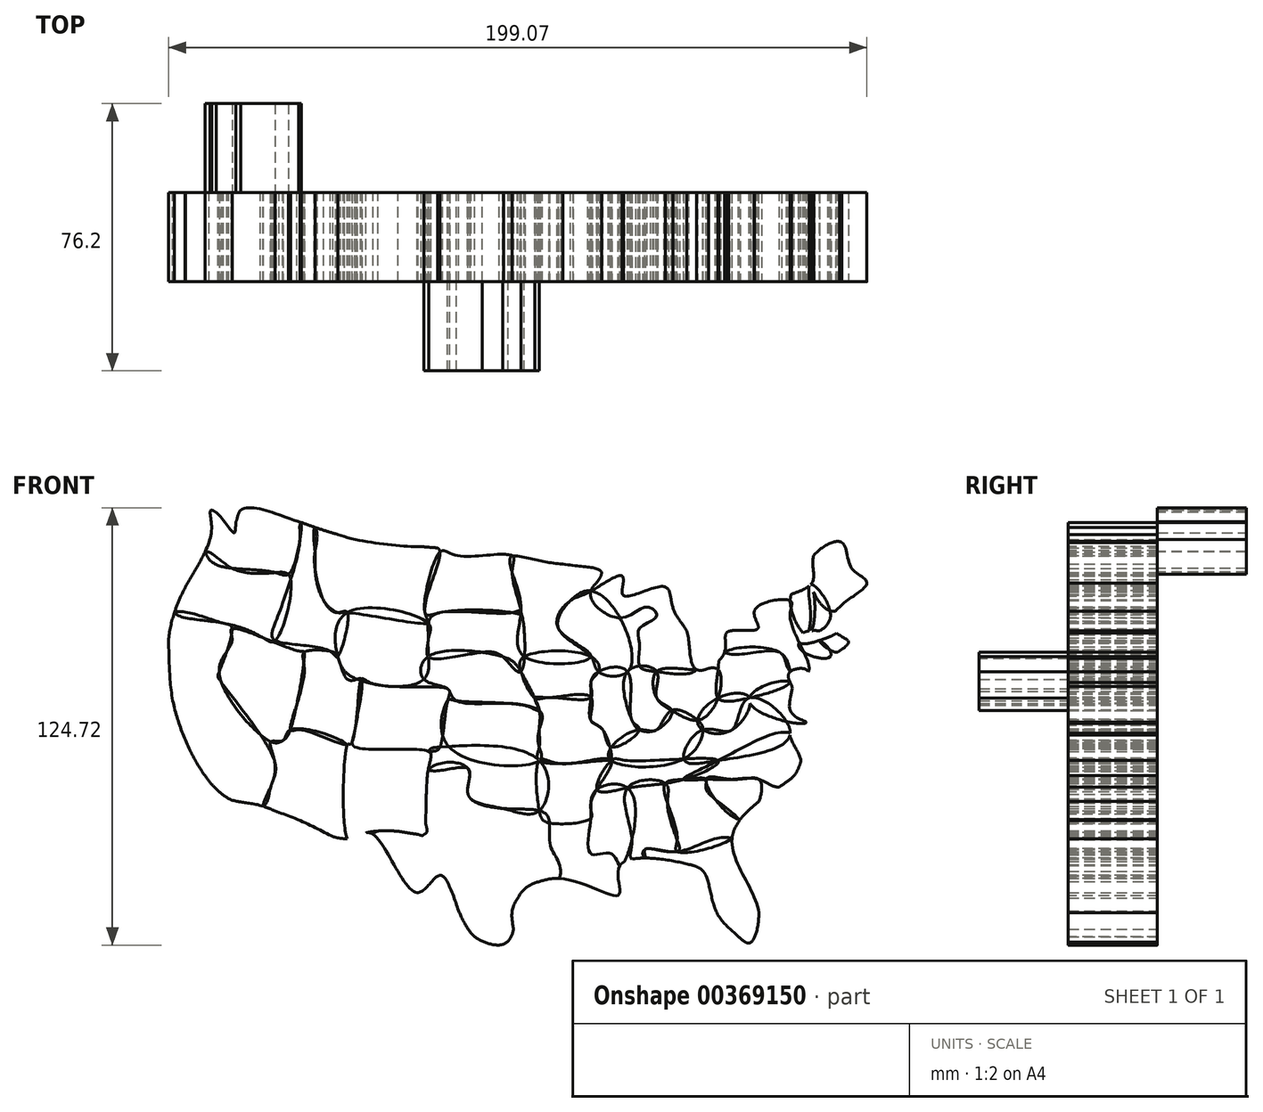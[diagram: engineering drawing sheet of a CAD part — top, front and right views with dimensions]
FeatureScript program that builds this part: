
annotation { "Feature Type Name" : "Feature", "Feature Type Description" : "" }
export const myFeature = defineFeature(function(context is Context, id is Id, definition is map)
    precondition{}
    {
        {
            var Q0;
            Q0=qCreatedBy(makeId("Front.planeOp"),FACE);
            var sketch = newSketch(context, id + "F0", { "sketchPlane" : qUnion([Q0])});
            skFitSpline(sketch, "E0", {"points": [v(64.5, -50.22) * mm, v(58.36, -43.46) * mm, v(55.29, -33.02) * mm, v(50.37, -29.64) * mm, v(30.71, -29.95) * mm, v(30.4, -38.24) * mm, v(13.2, -33.63) * mm, v(0, -42.85) * mm, v(0, -50.83) * mm, v(-10.75, -50.22) * mm, v(-20.58, -32.71) * mm, v(-27.03, -37.62) * mm, v(-39.62, -21.04) * mm, v(-47, -22.27) * mm, v(-70.95, -13.05) * mm, v(-80.78, -10.9) * mm, v(-90.3, 0) * mm, v(-96.75, 17.05) * mm, v(-97.98, 34.25) * mm, v(-93.06, 49.6) * mm, v(-85.7, 65.88) * mm, v(-85.7, 71.41) * mm, v(-79.24, 67.72) * mm, v(-77.4, 71.41) * mm, v(-56.2, 66.5) * mm, v(-32.56, 61.58) * mm, v(0, 58.51) * mm, v(14.44, 56.05) * mm, v(25.5, 53.6) * mm, v(22.42, 48.37) * mm, v(31.33, 52.67) * mm, v(31.64, 47.15) * mm, v(43.3, 49.6) * mm, v(45.76, 43.77) * mm, v(49.76, 37.01) * mm, v(52.52, 25.95) * mm, v(60.5, 30.87) * mm, v(61.43, 36.7) * mm, v(70.03, 37.62) * mm, v(69.1, 42.85) * mm, v(85.08, 50.22) * mm, v(86, 58.51) * mm, v(93.98, 62.2) * mm, v(96.75, 54.82) * mm, v(101.1, 50.52) * mm, v(92.14, 42.54) * mm, v(92.45, 36.4) * mm, v(95.83, 33.63) * mm, v(84.46, 25.34) * mm, v(82.93, 18.27) * mm, v(83.85, 10.9) * mm, v(79.24, 7.83) * mm, v(82.31, 0) * mm, v(76.17, -7.52) * mm, v(62.66, -22.27) * mm, v(70.34, -43.46) * mm, v(67.57, -52.06) * mm, v(64.5, -50.22) * mm]});
            skFitSpline(sketch, "E1", {"points": [v(-39.62, -21.04) * mm, v(-25.16, -21.04) * mm, v(-24.86, -17.35) * mm, v(-23.93, -2.61) * mm, v(-12.57, -2.3) * mm, v(-12.57, -9.67) * mm, v(-2.74, -13.67) * mm, v(7.7, -14.28) * mm, v(10.46, -16.74) * mm, v(10.77, -23.8) * mm, v(13.2, -29.02) * mm, v(13.2, -33.63) * mm, v(7.8, -34.54) * mm, v(1.66, -39.16) * mm, v(0.37, -48.1) * mm, v(-2.75, -52.46) * mm, v(-10.75, -50.22) * mm, v(-15.27, -42.85) * mm, v(-20.58, -32.71) * mm, v(-27.03, -37.62) * mm, v(-39.62, -21.04) * mm]});
            skFitSpline(sketch, "E2", {"points": [v(-47, -22.27) * mm, v(-47, 4.45) * mm, v(-44.82, 3.84) * mm, v(-23.93, 2.61) * mm, v(-23.93, -2.61) * mm, v(-25.16, -21.04) * mm, v(-27.03, -21.03) * mm, v(-43.02, -21.04) * mm, v(-47, -22.27) * mm]});
            skFitSpline(sketch, "E3", {"points": [v(-70.95, -13.05) * mm, v(-67.55, -2.61) * mm, v(-68.78, 5.37) * mm, v(-65.4, 5.68) * mm, v(-63.25, 8.75) * mm, v(-47, 4.45) * mm, v(-47.73, 0) * mm, v(-47, -22.27) * mm, v(-51.07, -21.72) * mm, v(-66.46, -14.89) * mm, v(-70.95, -13.05) * mm]});
            skFitSpline(sketch, "E4", {"points": [v(-67.79, 0) * mm, v(-83.52, 23.19) * mm, v(-83.52, 25.34) * mm, v(-79.83, 37.62) * mm, v(-82.3, 39.16) * mm, v(-96.29, 42.18) * mm, v(-97.98, 34.25) * mm, v(-96.75, 17.05) * mm, v(-90.3, 0) * mm, v(-80.78, -10.9) * mm, v(-70.95, -13.05) * mm, v(-68.78, -7.33) * mm, v(-67.79, 0) * mm]});
            skFitSpline(sketch, "E5", {"points": [v(-63.25, 8.75) * mm, v(-59.26, 30.87) * mm, v(-60.48, 31.17) * mm, v(-79.83, 37.62) * mm, v(-79.83, 34.25) * mm, v(-83.52, 25.34) * mm, v(-68.78, 5.37) * mm, v(-65.4, 5.68) * mm, v(-63.25, 8.75) * mm]});
            skFitSpline(sketch, "E6", {"points": [v(-67.55, 34.25) * mm, v(-63.25, 52.06) * mm, v(-67.55, 53.6) * mm, v(-79.83, 54.82) * mm, v(-87.53, 59.51) * mm, v(-93.06, 49.6) * mm, v(-96.29, 42.18) * mm, v(-82.3, 39.16) * mm, v(-70.95, 34.98) * mm, v(-67.55, 34.25) * mm]});
            skFitSpline(sketch, "E7", {"points": [v(-63.25, 53.6) * mm, v(-60.07, 67.88) * mm, v(-60.81, 68.15) * mm, v(-77.4, 71.41) * mm, v(-79.24, 64.96) * mm, v(-85.7, 71.41) * mm, v(-87.53, 59.51) * mm, v(-79.83, 54.82) * mm, v(-67.55, 53.6) * mm, v(-63.25, 53.6) * mm]});
            skFitSpline(sketch, "E8", {"points": [v(-60.07, 67.88) * mm, v(-56.2, 66.5) * mm, v(-56.2, 59.51) * mm, v(-56.2, 54.82) * mm, v(-53.73, 45.61) * mm, v(-49.73, 42.18) * mm, v(-47, 42.18) * mm, v(-49.73, 29.64) * mm, v(-51.88, 31.17) * mm, v(-67.55, 34.25) * mm, v(-67.55, 39.16) * mm, v(-60.48, 63.07) * mm, v(-60.07, 67.88) * mm]});
            skFitSpline(sketch, "E9", {"points": [v(-56.2, 66.5) * mm, v(-56.2, 59.51) * mm, v(-56.2, 54.82) * mm, v(-53.73, 45.61) * mm, v(-49.73, 42.18) * mm, v(-47, 42.18) * mm, v(-23.93, 39.16) * mm, v(-24.86, 42.18) * mm, v(-20.58, 59.51) * mm, v(-25.16, 60.94) * mm, v(-49.73, 64.48) * mm, v(-56.2, 66.5) * mm]});
            skFitSpline(sketch, "E10", {"points": [v(-49.73, 29.64) * mm, v(-51.88, 31.17) * mm, v(-59.26, 30.87) * mm, v(-59.26, 25.34) * mm, v(-63.25, 8.75) * mm, v(-60.48, 8.75) * mm, v(-47, 4.45) * mm, v(-44.82, 8.75) * mm, v(-42.98, 23.19) * mm, v(-44.2, 23.19) * mm, v(-47, 23.19) * mm, v(-49.73, 29.64) * mm]});
            skFitSpline(sketch, "E11", {"points": [v(-23.93, 39.16) * mm, v(-47, 42.18) * mm, v(-49.73, 29.64) * mm, v(-44.2, 23.19) * mm, v(-25.16, 23.19) * mm, v(-23.93, 34.25) * mm, v(-23.93, 39.16) * mm]});
            skFitSpline(sketch, "E12", {"points": [v(-23.93, 2.61) * mm, v(-44.82, 3.84) * mm, v(-44.82, 8.75) * mm, v(-42.98, 23.19) * mm, v(-39.62, 21.86) * mm, v(-18.4, 20.42) * mm, v(-18.4, 17.05) * mm, v(-20.58, 3.84) * mm, v(-23.93, 2.61) * mm]});
            skFitSpline(sketch, "E13", {"points": [v(-20.58, 3.84) * mm, v(-23.93, 2.61) * mm, v(-23.93, -2.61) * mm, v(-12.57, -2.3) * mm, v(-12.57, -9.67) * mm, v(-2.74, -13.67) * mm, v(7.7, -14.28) * mm, v(7.7, 0) * mm, v(-20.58, 3.84) * mm]});
            skFitSpline(sketch, "E14", {"points": [v(7.7, 0) * mm, v(-18.1, 4) * mm, v(-18.4, 17.05) * mm, v(-15.95, 17.05) * mm, v(7.7, 14.28) * mm, v(7.7, 8.75) * mm, v(7.7, 3.84) * mm, v(7.7, 0) * mm]});
            skFitSpline(sketch, "E15", {"points": [v(7.7, 14.28) * mm, v(2.48, 25.34) * mm, v(-2.74, 29.64) * mm, v(-23.93, 29.64) * mm, v(-25.16, 23.19) * mm, v(-18.4, 20.42) * mm, v(-15.95, 17.05) * mm, v(3.4, 15.78) * mm, v(7.7, 14.28) * mm]});
            skFitSpline(sketch, "E16", {"points": [v(2.48, 25.34) * mm, v(2.48, 42.18) * mm, v(0, 42.18) * mm, v(-20.58, 42.18) * mm, v(-23.93, 39.16) * mm, v(-23.93, 34.25) * mm, v(-23.93, 29.64) * mm, v(-15.95, 29.64) * mm, v(-8.52, 30.87) * mm, v(-2.74, 29.64) * mm, v(2.48, 25.34) * mm]});
            skFitSpline(sketch, "E17", {"points": [v(2.48, 42.18) * mm, v(0, 42.18) * mm, v(-20.58, 42.18) * mm, v(-24.86, 42.18) * mm, v(-20.58, 59.51) * mm, v(-15.95, 58.51) * mm, v(0, 58.51) * mm, v(0, 53.6) * mm, v(2.48, 42.18) * mm]});
            skFitSpline(sketch, "E18", {"points": [v(25.5, 53.6) * mm, v(22.42, 48.37) * mm, v(16.6, 45.61) * mm, v(13.2, 37.62) * mm, v(22.42, 29.64) * mm, v(3.52, 29.64) * mm, v(2.48, 42.18) * mm, v(0, 53.6) * mm, v(0, 58.51) * mm, v(14.44, 56.05) * mm, v(25.5, 53.6) * mm]});
            skFitSpline(sketch, "E19", {"points": [v(22.42, 29.64) * mm, v(3.52, 29.64) * mm, v(2.48, 25.34) * mm, v(6.44, 17.86) * mm, v(10.46, 17.97) * mm, v(22.42, 17.97) * mm, v(22.42, 22.27) * mm, v(24.6, 25.34) * mm, v(22.42, 29.64) * mm]});
            skFitSpline(sketch, "E20", {"points": [v(22.42, 17.97) * mm, v(10.46, 17.97) * mm, v(6.44, 17.86) * mm, v(7.7, 14.28) * mm, v(7.7, 8.75) * mm, v(7.7, 3.84) * mm, v(7.7, 0) * mm, v(25.82, 0) * mm, v(27.97, 0) * mm, v(28.28, 0) * mm, v(25.82, 8.75) * mm, v(22.42, 11.52) * mm, v(22.42, 17.97) * mm]});
            skFitSpline(sketch, "E21", {"points": [v(28.28, 0) * mm, v(22.42, -12.13) * mm, v(22.42, -16.43) * mm, v(10.63, -17.8) * mm, v(7.7, -14.28) * mm, v(7.7, 0) * mm, v(13.88, -0.9) * mm, v(28.28, 0) * mm]});
            skFitSpline(sketch, "E22", {"points": [v(22.42, -16.43) * mm, v(22.42, -26.57) * mm, v(28.28, -26.57) * mm, v(30.71, -29.95) * mm, v(34.11, -22.57) * mm, v(32.89, -7.83) * mm, v(24.2, -8.17) * mm, v(22.42, -12.13) * mm, v(22.42, -16.43) * mm]});
            skFitSpline(sketch, "E23", {"points": [v(28.28, 0) * mm, v(24.2, -8.17) * mm, v(32.89, -7.83) * mm, v(48.86, -5.37) * mm, v(58.69, 0) * mm, v(32.89, 0) * mm, v(28.28, 0) * mm]});
            skFitSpline(sketch, "E24", {"points": [v(43.63, -6.51) * mm, v(32.89, -7.83) * mm, v(34.11, -22.57) * mm, v(34.11, -28.12) * mm, v(37.8, -27.8) * mm, v(37.8, -25.34) * mm, v(47.01, -25.95) * mm, v(47.01, -22.57) * mm, v(44.25, -12.13) * mm, v(43.63, -6.51) * mm]});
            skFitSpline(sketch, "E25", {"points": [v(48.9, 0.47) * mm, v(28.28, 0) * mm, v(28.28, 3.84) * mm, v(36.26, 8.75) * mm, v(41.18, 8.75) * mm, v(45.48, 14.28) * mm, v(52.85, 11.52) * mm, v(54.39, 8.75) * mm, v(48.9, 0.47) * mm]});
            skFitSpline(sketch, "E26", {"points": [v(24.6, 25.34) * mm, v(22.42, 22.27) * mm, v(22.42, 17.97) * mm, v(22.42, 11.52) * mm, v(25.82, 8.75) * mm, v(28.28, 3.84) * mm, v(36.26, 8.75) * mm, v(34.11, 11.52) * mm, v(32.89, 25.34) * mm, v(24.6, 25.34) * mm]});
            skFitSpline(sketch, "E27", {"points": [v(32.89, 25.34) * mm, v(24.6, 25.34) * mm, v(22.42, 29.64) * mm, v(13.2, 37.62) * mm, v(16.6, 45.61) * mm, v(22.42, 48.37) * mm, v(30.71, 40.7) * mm, v(32.89, 25.34) * mm]});
            skFitSpline(sketch, "E28", {"points": [v(45.48, 14.28) * mm, v(41.18, 8.75) * mm, v(36.26, 8.75) * mm, v(34.11, 11.52) * mm, v(32.89, 25.34) * mm, v(41.18, 25.34) * mm, v(41.18, 17.86) * mm, v(45.48, 14.28) * mm]});
            skFitSpline(sketch, "E29", {"points": [v(41.18, 25.34) * mm, v(36.26, 26.95) * mm, v(36.26, 33.32) * mm, v(36.26, 37.62) * mm, v(41.18, 41.31) * mm, v(38.41, 43.77) * mm, v(30.71, 40.7) * mm, v(22.42, 48.37) * mm, v(31.33, 52.67) * mm, v(31.64, 47.15) * mm, v(43.3, 49.6) * mm, v(45.76, 43.77) * mm, v(49.76, 37.01) * mm, v(52.52, 25.95) * mm, v(41.18, 25.34) * mm]});
            skFitSpline(sketch, "E30", {"points": [v(52.85, 11.52) * mm, v(45.48, 14.28) * mm, v(41.18, 17.86) * mm, v(41.18, 25.34) * mm, v(52.52, 25.95) * mm, v(58.69, 25.95) * mm, v(58.69, 17.86) * mm, v(52.85, 11.52) * mm]});
            skFitSpline(sketch, "E31", {"points": [v(47.01, -25.95) * mm, v(37.8, -25.34) * mm, v(37.8, -27.8) * mm, v(50.37, -29.64) * mm, v(55.29, -33.02) * mm, v(58.36, -43.46) * mm, v(64.5, -50.22) * mm, v(67.57, -52.06) * mm, v(70.34, -43.46) * mm, v(62.66, -22.27) * mm, v(47.01, -25.95) * mm]});
            skFitSpline(sketch, "E32", {"points": [v(47.01, -25.95) * mm, v(47.01, -22.57) * mm, v(44.25, -12.13) * mm, v(43.63, -6.51) * mm, v(48.86, -5.37) * mm, v(55.29, -5.37) * mm, v(55.29, -8.17) * mm, v(64.5, -16.74) * mm, v(62.66, -22.27) * mm, v(47.01, -25.95) * mm]});
            skFitSpline(sketch, "E33", {"points": [v(64.5, -16.74) * mm, v(55.29, -5.37) * mm, v(62.66, -5.37) * mm, v(70.34, -5.37) * mm, v(70.34, -11.67) * mm, v(64.5, -16.74) * mm]});
            skFitSpline(sketch, "E34", {"points": [v(58.69, 0) * mm, v(48.86, -5.37) * mm, v(55.29, -5.37) * mm, v(62.66, -5.37) * mm, v(70.34, -5.37) * mm, v(76.17, -7.52) * mm, v(82.31, 0) * mm, v(79.24, 7.83) * mm, v(58.69, 0) * mm]});
            skFitSpline(sketch, "E35", {"points": [v(79.24, 7.83) * mm, v(58.69, 0) * mm, v(48.9, 0.47) * mm, v(54.39, 8.75) * mm, v(62.66, 8.75) * mm, v(67.57, 17.86) * mm, v(79.24, 7.83) * mm]});
            skFitSpline(sketch, "E36", {"points": [v(67.57, 17.86) * mm, v(58.69, 17.86) * mm, v(52.85, 11.52) * mm, v(54.39, 8.75) * mm, v(62.66, 8.75) * mm, v(67.57, 17.86) * mm]});
            skFitSpline(sketch, "E37", {"points": [v(67.57, 17.86) * mm, v(79.24, 22.27) * mm, v(79.24, 14.28) * mm, v(83.85, 10.9) * mm, v(79.24, 10.9) * mm, v(67.57, 17.86) * mm]});
            skFitSpline(sketch, "E38", {"points": [v(79.24, 22.27) * mm, v(67.57, 17.86) * mm, v(58.69, 17.86) * mm, v(58.69, 25.95) * mm, v(60.5, 30.87) * mm, v(76.17, 30.87) * mm, v(79.24, 25.34) * mm, v(79.24, 22.27) * mm]});
            skFitSpline(sketch, "E39", {"points": [v(84.46, 25.34) * mm, v(82.93, 18.27) * mm, v(79.24, 22.27) * mm, v(79.24, 25.34) * mm, v(84.46, 25.34) * mm]});
            skFitSpline(sketch, "E40", {"points": [v(79.24, 45.61) * mm, v(69.1, 42.85) * mm, v(70.03, 37.62) * mm, v(61.43, 36.7) * mm, v(60.5, 30.87) * mm, v(76.17, 30.87) * mm, v(79.24, 25.34) * mm, v(84.46, 25.34) * mm, v(79.24, 40.7) * mm, v(79.24, 45.61) * mm]});
            skFitSpline(sketch, "E41", {"points": [v(81.82, 33.68) * mm, v(87.56, 34.25) * mm, v(90.67, 29.64) * mm, v(83.17, 30.87) * mm, v(81.82, 33.68) * mm]});
            skFitSpline(sketch, "E42", {"points": [v(92.68, 30.87) * mm, v(90.67, 34.25) * mm, v(87.56, 34.25) * mm, v(92.68, 30.87) * mm]});
            skFitSpline(sketch, "E43", {"points": [v(92.45, 36.4) * mm, v(90.67, 36.7) * mm, v(82.93, 36.4) * mm, v(81.82, 33.68) * mm, v(87.56, 34.25) * mm, v(92.45, 36.4) * mm]});
            skFitSpline(sketch, "E44", {"points": [v(85.08, 50.22) * mm, v(85.08, 36.4) * mm, v(82.93, 36.4) * mm, v(79.24, 45.61) * mm, v(81.82, 50.22) * mm, v(85.08, 50.22) * mm]});
            skFitSpline(sketch, "E45", {"points": [v(85.08, 36.4) * mm, v(90.67, 40.7) * mm, v(85.08, 50.22) * mm, v(85.08, 40.7) * mm, v(85.08, 36.4) * mm]});
            skFitSpline(sketch, "E46", {"points": [v(85.08, 50.22) * mm, v(86, 58.51) * mm, v(93.98, 62.2) * mm, v(96.75, 54.82) * mm, v(101.1, 50.52) * mm, v(92.14, 42.54) * mm, v(85.08, 50.22) * mm]});
            skSolve(sketch);
        }
        {
            var Q0;
            {var subQ0=sQuery(id+"F0.wireOp",EDGE,"E7");var subQ4=sQuery(id+"F0.wireOp",EDGE,"E0");var subQ6=makeQuery(id+"F0.imprint","INTERSECT",VERTEX,{"disambiguationData":[OD(1.0)],"derivedFrom":[subQ4,subQ0]});Q0=makeQuery(id+"F0.imprint","IMPRINT",FACE,{"disambiguationData":[TD([[makeQuery(id+"F0.imprint","IMPRINT",EDGE,{"disambiguationData":[TD([[subQ6,-1.0]])],"derivedFrom":subQ4}),-1.0]])]});}
            extrude(context, id + "F1", {"entities" : qUnion([Q0]), "oppositeDirection" : true, "depth" : 25.4 * mm});
        }
        {
            var Q0;
            {var subQ0=sQuery(id+"F0.wireOp",EDGE,"E6");var subQ14=sQuery(id+"F0.wireOp",EDGE,"E5");var subQ16=makeQuery(id+"F0.imprint","INTERSECT",VERTEX,{"disambiguationData":[OD(0.0)],"derivedFrom":[subQ14,subQ0]});Q0=makeQuery(id+"F0.imprint","IMPRINT",FACE,{"disambiguationData":[TD([[makeQuery(id+"F0.imprint","IMPRINT",EDGE,{"disambiguationData":[TD([[subQ16,-1.0]])],"derivedFrom":subQ14}),-1.0]])]});}
            extrude(context, id + "F2", {"entities" : qUnion([Q0]), "depth" : 25.4 * mm});
        }
        {
            var Q0;
            {var subQ0=sQuery(id+"F0.wireOp",EDGE,"E4");var subQ6=sQuery(id+"F0.wireOp",EDGE,"E0");var subQ15=makeQuery(id+"F0.imprint","INTERSECT",VERTEX,{"disambiguationData":[OD(1.0)],"derivedFrom":[subQ6,subQ0]});Q0=makeQuery(id+"F0.imprint","IMPRINT",FACE,{"disambiguationData":[TD([[makeQuery(id+"F0.imprint","IMPRINT",EDGE,{"disambiguationData":[TD([[subQ15,-1.0]])],"derivedFrom":subQ6}),-1.0]])]});}
            extrude(context, id + "F3", {"entities" : qUnion([Q0]), "depth" : 25.4 * mm});
        }
        {
            var Q0;
            {var subQ1=sQuery(id+"F0.wireOp",EDGE,"E5");var subQ13=sQuery(id+"F0.wireOp",EDGE,"E3");var subQ14=makeQuery(id+"F0.imprint","INTERSECT",VERTEX,{"disambiguationData":[OD(0.0)],"derivedFrom":[subQ13,subQ1]});Q0=makeQuery(id+"F0.imprint","IMPRINT",FACE,{"disambiguationData":[TD([[makeQuery(id+"F0.imprint","IMPRINT",EDGE,{"disambiguationData":[TD([[subQ14,-1.0]])],"derivedFrom":subQ13}),1.0]])]});}
            extrude(context, id + "F4", {"entities" : qUnion([Q0]), "depth" : 25.4 * mm});
        }
        {
            var Q0;
            {var subQ1=sQuery(id+"F0.wireOp",EDGE,"E8");var subQ7=sQuery(id+"F0.wireOp",EDGE,"E6");var subQ17=makeQuery(id+"F0.imprint","INTERSECT",VERTEX,{"disambiguationData":[OD(0.0)],"derivedFrom":[subQ7,subQ1]});Q0=makeQuery(id+"F0.imprint","IMPRINT",FACE,{"disambiguationData":[TD([[makeQuery(id+"F0.imprint","IMPRINT",EDGE,{"disambiguationData":[TD([[subQ17,1.0]])],"derivedFrom":subQ7}),-1.0]])]});}
            extrude(context, id + "F5", {"entities" : qUnion([Q0]), "depth" : 25.4 * mm});
        }
        {
            var Q0;
            {var subQ0=sQuery(id+"F0.wireOp",EDGE,"E4");var subQ1=sQuery(id+"F0.wireOp",EDGE,"E3");var subQ2=makeQuery(id+"F0.imprint","INTERSECT",VERTEX,{"disambiguationData":[OD(0.0)],"derivedFrom":[subQ1,subQ0]});Q0=makeQuery(id+"F0.imprint","IMPRINT",FACE,{"disambiguationData":[TD([[makeQuery(id+"F0.imprint","IMPRINT",EDGE,{"disambiguationData":[TD([[subQ2,-1.0]])],"derivedFrom":subQ1}),-1.0]])]});}
            extrude(context, id + "F6", {"entities" : qUnion([Q0]), "depth" : 25.4 * mm});
        }
        {
            var Q0;
            {var subQ1=sQuery(id+"F0.wireOp",EDGE,"E10");var subQ7=sQuery(id+"F0.wireOp",EDGE,"E5");var subQ8=makeQuery(id+"F0.imprint","INTERSECT",VERTEX,{"disambiguationData":[OD(1.0)],"derivedFrom":[subQ7,subQ1]});Q0=makeQuery(id+"F0.imprint","IMPRINT",FACE,{"disambiguationData":[TD([[makeQuery(id+"F0.imprint","IMPRINT",EDGE,{"disambiguationData":[TD([[subQ8,-1.0]])],"derivedFrom":subQ7}),-1.0]])]});}
            extrude(context, id + "F7", {"entities" : qUnion([Q0]), "depth" : 25.4 * mm});
        }
        {
            var Q0;
            {var subQ0=sQuery(id+"F0.wireOp",EDGE,"E9");var subQ1=sQuery(id+"F0.wireOp",EDGE,"E0");var subQ18=makeQuery(id+"F0.imprint","INTERSECT",VERTEX,{"disambiguationData":[OD(1.0)],"derivedFrom":[subQ1,subQ0]});Q0=makeQuery(id+"F0.imprint","IMPRINT",FACE,{"disambiguationData":[TD([[makeQuery(id+"F0.imprint","IMPRINT",EDGE,{"disambiguationData":[TD([[subQ18,-1.0]])],"derivedFrom":subQ1}),-1.0]])]});}
            extrude(context, id + "F8", {"entities" : qUnion([Q0]), "depth" : 25.4 * mm});
        }
        {
            var Q0;
            {var subQ0=sQuery(id+"F0.wireOp",EDGE,"E2");var subQ10=sQuery(id+"F0.wireOp",EDGE,"E0");var subQ11=makeQuery(id+"F0.imprint","INTERSECT",VERTEX,{"disambiguationData":[OD(0.0)],"derivedFrom":[subQ10,subQ0]});Q0=makeQuery(id+"F0.imprint","IMPRINT",FACE,{"disambiguationData":[TD([[makeQuery(id+"F0.imprint","IMPRINT",EDGE,{"disambiguationData":[TD([[subQ11,1.0]])],"derivedFrom":subQ10}),-1.0]])]});}
            extrude(context, id + "F9", {"entities" : qUnion([Q0]), "operationType" : NewBodyOperationType.ADD, "depth" : 25.4 * mm});
        }
        {
            var Q0;
            {var subQ0=sQuery(id+"F0.wireOp",EDGE,"E13");var subQ2=sQuery(id+"F0.wireOp",EDGE,"E1");var subQ6=makeQuery(id+"F0.imprint","INTERSECT",VERTEX,{"disambiguationData":[OD(1.0)],"derivedFrom":[subQ2,subQ0]});Q0=makeQuery(id+"F0.imprint","IMPRINT",FACE,{"disambiguationData":[TD([[makeQuery(id+"F0.imprint","IMPRINT",EDGE,{"disambiguationData":[TD([[subQ6,-1.0]])],"derivedFrom":subQ2}),1.0]])]});}
            extrude(context, id + "F10", {"entities" : qUnion([Q0]), "depth" : 25.4 * mm});
        }
        {
            var Q0;
            {var subQ0=sQuery(id+"F0.wireOp",EDGE,"E14");var subQ1=sQuery(id+"F0.wireOp",EDGE,"E12");var subQ2=makeQuery(id+"F0.imprint","INTERSECT",VERTEX,{"disambiguationData":[OD(0.0)],"derivedFrom":[subQ1,subQ0]});Q0=makeQuery(id+"F0.imprint","IMPRINT",FACE,{"disambiguationData":[TD([[makeQuery(id+"F0.imprint","IMPRINT",EDGE,{"disambiguationData":[TD([[subQ2,-1.0]])],"derivedFrom":subQ1}),1.0]])]});}
            extrude(context, id + "F11", {"entities" : qUnion([Q0]), "depth" : 25.4 * mm});
        }
        {
            var Q0;
            {var subQ1=sQuery(id+"F0.wireOp",EDGE,"E11");var subQ3=sQuery(id+"F0.wireOp",EDGE,"E15");var subQ11=makeQuery(id+"F0.imprint","INTERSECT",VERTEX,{"disambiguationData":[OD(0.0)],"derivedFrom":[subQ1,subQ3]});Q0=makeQuery(id+"F0.imprint","IMPRINT",FACE,{"disambiguationData":[TD([[makeQuery(id+"F0.imprint","IMPRINT",EDGE,{"disambiguationData":[TD([[subQ11,-1.0]])],"derivedFrom":subQ1}),-1.0]])]});}
            extrude(context, id + "F12", {"entities" : qUnion([Q0]), "depth" : 25.4 * mm});
        }
        {
            var Q0;
            {var subQ1=sQuery(id+"F0.wireOp",EDGE,"E11");var subQ13=sQuery(id+"F0.wireOp",EDGE,"E15");var subQ16=makeQuery(id+"F0.imprint","INTERSECT",VERTEX,{"disambiguationData":[OD(1.0)],"derivedFrom":[subQ1,subQ13]});Q0=makeQuery(id+"F0.imprint","IMPRINT",FACE,{"disambiguationData":[TD([[makeQuery(id+"F0.imprint","IMPRINT",EDGE,{"disambiguationData":[TD([[subQ16,-1.0]])],"derivedFrom":subQ1}),-1.0]])]});}
            extrude(context, id + "F13", {"entities" : qUnion([Q0]), "depth" : 25.4 * mm});
        }
        {
            var Q0;
            Q0=makeQuery(id+"F12.opExtrude","CAP_FACE",FACE,{"disambiguationData":[OSD([sQuery(id+"F0.wireOp",EDGE,"E11"),sQuery(id+"F0.wireOp",EDGE,"E12"),sQuery(id+"F0.wireOp",EDGE,"E14"),sQuery(id+"F0.wireOp",EDGE,"E15"),sQuery(id+"F0.wireOp",EDGE,"E16"),sQuery(id+"F0.wireOp",EDGE,"E19"),sQuery(id+"F0.wireOp",EDGE,"E20")])],"isStart":false});
            extrude(context, id + "F14", {"entities" : qUnion([Q0]), "depth" : 25.4 * mm});
        }
        {
            var Q0;
            {var subQ1=sQuery(id+"F0.wireOp",EDGE,"E20");var subQ13=sQuery(id+"F0.wireOp",EDGE,"E14");var subQ15=makeQuery(id+"F0.imprint","INTERSECT",VERTEX,{"disambiguationData":[OD(1.0)],"derivedFrom":[subQ13,subQ1]});Q0=makeQuery(id+"F0.imprint","IMPRINT",FACE,{"disambiguationData":[TD([[makeQuery(id+"F0.imprint","IMPRINT",EDGE,{"disambiguationData":[TD([[subQ15,-1.0]])],"derivedFrom":subQ13}),1.0]])]});}
            extrude(context, id + "F15", {"entities" : qUnion([Q0]), "depth" : 25.4 * mm});
        }
        {
            var Q0;
            {var subQ0=sQuery(id+"F0.wireOp",EDGE,"E18");var subQ6=sQuery(id+"F0.wireOp",EDGE,"E0");var subQ15=makeQuery(id+"F0.imprint","INTERSECT",VERTEX,{"disambiguationData":[OD(1.0)],"derivedFrom":[subQ6,subQ0]});Q0=makeQuery(id+"F0.imprint","IMPRINT",FACE,{"disambiguationData":[TD([[makeQuery(id+"F0.imprint","IMPRINT",EDGE,{"disambiguationData":[TD([[subQ15,-1.0]])],"derivedFrom":subQ6}),-1.0]])]});}
            extrude(context, id + "F16", {"entities" : qUnion([Q0]), "depth" : 25.4 * mm});
        }
        {
            var Q0;
            {var subQ0=sQuery(id+"F0.wireOp",EDGE,"E22");var subQ1=sQuery(id+"F0.wireOp",EDGE,"E0");var subQ9=makeQuery(id+"F0.imprint","INTERSECT",VERTEX,{"disambiguationData":[OD(0.0)],"derivedFrom":[subQ1,subQ0]});Q0=makeQuery(id+"F0.imprint","IMPRINT",FACE,{"disambiguationData":[TD([[makeQuery(id+"F0.imprint","IMPRINT",EDGE,{"disambiguationData":[TD([[subQ9,-1.0]])],"derivedFrom":subQ1}),-1.0]])]});}
            extrude(context, id + "F17", {"entities" : qUnion([Q0]), "depth" : 25.4 * mm});
        }
        {
            var Q0;
            {var subQ1=sQuery(id+"F0.wireOp",EDGE,"E26");var subQ4=sQuery(id+"F0.wireOp",EDGE,"E20");var subQ5=makeQuery(id+"F0.imprint","INTERSECT",VERTEX,{"disambiguationData":[OD(0.0)],"derivedFrom":[subQ4,subQ1]});Q0=makeQuery(id+"F0.imprint","IMPRINT",FACE,{"disambiguationData":[TD([[makeQuery(id+"F0.imprint","IMPRINT",EDGE,{"disambiguationData":[TD([[subQ5,-1.0]])],"derivedFrom":subQ4}),-1.0]])]});}
            extrude(context, id + "F18", {"entities" : qUnion([Q0]), "depth" : 25.4 * mm});
        }
        {
            var Q0;
            {var subQ0=sQuery(id+"F0.wireOp",EDGE,"E27");var subQ6=sQuery(id+"F0.wireOp",EDGE,"E18");var subQ12=makeQuery(id+"F0.imprint","INTERSECT",VERTEX,{"disambiguationData":[OD(0.0)],"derivedFrom":[subQ6,subQ0]});Q0=makeQuery(id+"F0.imprint","IMPRINT",FACE,{"disambiguationData":[TD([[makeQuery(id+"F0.imprint","IMPRINT",EDGE,{"disambiguationData":[TD([[subQ12,1.0]])],"derivedFrom":subQ0}),-1.0]])]});}
            extrude(context, id + "F19", {"entities" : qUnion([Q0]), "depth" : 25.4 * mm});
        }
        {
            var Q0;
            {var subQ0=sQuery(id+"F0.wireOp",EDGE,"E29");var subQ5=sQuery(id+"F0.wireOp",EDGE,"E0");var subQ10=makeQuery(id+"F0.imprint","INTERSECT",VERTEX,{"disambiguationData":[OD(0.0)],"derivedFrom":[subQ5,subQ0]});Q0=makeQuery(id+"F0.imprint","IMPRINT",FACE,{"disambiguationData":[TD([[makeQuery(id+"F0.imprint","IMPRINT",EDGE,{"disambiguationData":[TD([[subQ10,1.0]])],"derivedFrom":subQ5}),-1.0]])]});}
            extrude(context, id + "F20", {"entities" : qUnion([Q0]), "depth" : 25.4 * mm});
        }
        {
            var Q0;
            {var subQ0=sQuery(id+"F0.wireOp",EDGE,"E28");var subQ11=sQuery(id+"F0.wireOp",EDGE,"E25");var subQ12=makeQuery(id+"F0.imprint","INTERSECT",VERTEX,{"disambiguationData":[OD(0.0)],"derivedFrom":[subQ11,subQ0]});Q0=makeQuery(id+"F0.imprint","IMPRINT",FACE,{"disambiguationData":[TD([[makeQuery(id+"F0.imprint","IMPRINT",EDGE,{"disambiguationData":[TD([[subQ12,1.0]])],"derivedFrom":subQ0}),-1.0]])]});}
            extrude(context, id + "F21", {"entities" : qUnion([Q0]), "depth" : 25.4 * mm});
        }
        {
            var Q0;
            {var subQ0=sQuery(id+"F0.wireOp",EDGE,"E30");var subQ1=sQuery(id+"F0.wireOp",EDGE,"E28");var subQ7=makeQuery(id+"F0.imprint","INTERSECT",VERTEX,{"disambiguationData":[OD(0.0)],"derivedFrom":[subQ1,subQ0]});Q0=makeQuery(id+"F0.imprint","IMPRINT",FACE,{"disambiguationData":[TD([[makeQuery(id+"F0.imprint","IMPRINT",EDGE,{"disambiguationData":[TD([[subQ7,1.0]])],"derivedFrom":subQ0}),-1.0]])]});}
            extrude(context, id + "F22", {"entities" : qUnion([Q0]), "depth" : 25.4 * mm});
        }
        {
            var Q0;
            {var subQ1=sQuery(id+"F0.wireOp",EDGE,"E25");var subQ4=sQuery(id+"F0.wireOp",EDGE,"E20");var subQ5=makeQuery(id+"F0.imprint","INTERSECT",VERTEX,{"derivedFrom":[subQ4,subQ1]});Q0=makeQuery(id+"F0.imprint","IMPRINT",FACE,{"disambiguationData":[TD([[makeQuery(id+"F0.imprint","IMPRINT",EDGE,{"disambiguationData":[TD([[subQ5,-1.0]])],"derivedFrom":subQ1}),-1.0]])]});}
            extrude(context, id + "F23", {"entities" : qUnion([Q0]), "depth" : 25.4 * mm});
        }
        {
            var Q0;
            {var subQ1=sQuery(id+"F0.wireOp",EDGE,"E23");var subQ2=sQuery(id+"F0.wireOp",EDGE,"E22");var subQ8=sQuery(id+"F0.wireOp",EDGE,"E21");var subQ9=makeQuery(id+"F0.imprint","INTERSECT",VERTEX,{"derivedFrom":[subQ8,subQ2,subQ1]});Q0=makeQuery(id+"F0.imprint","IMPRINT",FACE,{"disambiguationData":[TD([[makeQuery(id+"F0.imprint","IMPRINT",EDGE,{"disambiguationData":[TD([[subQ9,1.0]])],"derivedFrom":subQ2}),-1.0]])]});}
            extrude(context, id + "F24", {"entities" : qUnion([Q0]), "depth" : 25.4 * mm});
        }
        {
            var Q0;
            {var subQ1=sQuery(id+"F0.wireOp",EDGE,"E24");var subQ3=sQuery(id+"F0.wireOp",EDGE,"E0");var subQ16=makeQuery(id+"F0.imprint","INTERSECT",VERTEX,{"derivedFrom":[subQ3,subQ1]});Q0=makeQuery(id+"F0.imprint","IMPRINT",FACE,{"disambiguationData":[TD([[makeQuery(id+"F0.imprint","IMPRINT",EDGE,{"disambiguationData":[TD([[subQ16,1.0]])],"derivedFrom":subQ1}),1.0]])]});}
            extrude(context, id + "F25", {"entities" : qUnion([Q0]), "depth" : 25.4 * mm});
        }
        {
            var Q0;
            {var subQ0=sQuery(id+"F0.wireOp",EDGE,"E31");var subQ6=sQuery(id+"F0.wireOp",EDGE,"E0");var subQ12=makeQuery(id+"F0.imprint","INTERSECT",VERTEX,{"disambiguationData":[OD(0.0)],"derivedFrom":[subQ6,subQ0]});Q0=makeQuery(id+"F0.imprint","IMPRINT",FACE,{"disambiguationData":[TD([[makeQuery(id+"F0.imprint","IMPRINT",EDGE,{"disambiguationData":[TD([[subQ12,1.0]])],"derivedFrom":subQ6}),-1.0]])]});}
            extrude(context, id + "F26", {"entities" : qUnion([Q0]), "depth" : 25.4 * mm});
        }
        {
            var Q0;
            {var subQ1=sQuery(id+"F0.wireOp",EDGE,"E32");var subQ11=sQuery(id+"F0.wireOp",EDGE,"E24");var subQ17=makeQuery(id+"F0.imprint","INTERSECT",VERTEX,{"disambiguationData":[OD(0.0)],"derivedFrom":[subQ11,subQ1]});Q0=makeQuery(id+"F0.imprint","IMPRINT",FACE,{"disambiguationData":[TD([[makeQuery(id+"F0.imprint","IMPRINT",EDGE,{"disambiguationData":[TD([[subQ17,-1.0]])],"derivedFrom":subQ1}),-1.0]])]});}
            extrude(context, id + "F27", {"entities" : qUnion([Q0]), "depth" : 25.4 * mm});
        }
        {
            var Q0;
            {var subQ0=sQuery(id+"F0.wireOp",EDGE,"E33");var subQ5=sQuery(id+"F0.wireOp",EDGE,"E0");var subQ6=makeQuery(id+"F0.imprint","INTERSECT",VERTEX,{"disambiguationData":[OD(0.0)],"derivedFrom":[subQ5,subQ0]});Q0=makeQuery(id+"F0.imprint","IMPRINT",FACE,{"disambiguationData":[TD([[makeQuery(id+"F0.imprint","IMPRINT",EDGE,{"disambiguationData":[TD([[subQ6,-1.0]])],"derivedFrom":subQ5}),-1.0]])]});}
            extrude(context, id + "F28", {"entities" : qUnion([Q0]), "depth" : 25.4 * mm});
        }
        {
            var Q0;
            {var subQ0=sQuery(id+"F0.wireOp",EDGE,"E36");var subQ1=sQuery(id+"F0.wireOp",EDGE,"E35");var subQ2=makeQuery(id+"F0.imprint","INTERSECT",VERTEX,{"disambiguationData":[OD(0.0)],"derivedFrom":[subQ1,subQ0]});Q0=makeQuery(id+"F0.imprint","IMPRINT",FACE,{"disambiguationData":[TD([[makeQuery(id+"F0.imprint","IMPRINT",EDGE,{"disambiguationData":[TD([[subQ2,-1.0]])],"derivedFrom":subQ1}),-1.0]])]});}
            extrude(context, id + "F29", {"entities" : qUnion([Q0]), "depth" : 25.4 * mm});
        }
        {
            var Q0;
            {var subQ0=sQuery(id+"F0.wireOp",EDGE,"E34");var subQ6=sQuery(id+"F0.wireOp",EDGE,"E0");var subQ11=makeQuery(id+"F0.imprint","INTERSECT",VERTEX,{"disambiguationData":[OD(0.0)],"derivedFrom":[subQ6,subQ0]});Q0=makeQuery(id+"F0.imprint","IMPRINT",FACE,{"disambiguationData":[TD([[makeQuery(id+"F0.imprint","IMPRINT",EDGE,{"disambiguationData":[TD([[subQ11,1.0]])],"derivedFrom":subQ6}),-1.0]])]});}
            extrude(context, id + "F30", {"entities" : qUnion([Q0]), "depth" : 25.4 * mm});
        }
        {
            var Q0;
            {var subQ0=sQuery(id+"F0.wireOp",EDGE,"E36");var subQ1=sQuery(id+"F0.wireOp",EDGE,"E35");var subQ5=makeQuery(id+"F0.imprint","INTERSECT",VERTEX,{"disambiguationData":[OD(0.0)],"derivedFrom":[subQ1,subQ0]});Q0=makeQuery(id+"F0.imprint","IMPRINT",FACE,{"disambiguationData":[TD([[makeQuery(id+"F0.imprint","IMPRINT",EDGE,{"disambiguationData":[TD([[subQ5,-1.0]])],"derivedFrom":subQ0}),1.0]])]});}
            extrude(context, id + "F31", {"entities" : qUnion([Q0]), "depth" : 25.4 * mm});
        }
        {
            var Q0;
            {var subQ1=sQuery(id+"F0.wireOp",EDGE,"E38");var subQ6=sQuery(id+"F0.wireOp",EDGE,"E0");var subQ7=makeQuery(id+"F0.imprint","INTERSECT",VERTEX,{"derivedFrom":[subQ6,subQ1]});Q0=makeQuery(id+"F0.imprint","IMPRINT",FACE,{"disambiguationData":[TD([[makeQuery(id+"F0.imprint","IMPRINT",EDGE,{"disambiguationData":[TD([[subQ7,1.0]])],"derivedFrom":subQ1}),-1.0]])]});}
            extrude(context, id + "F32", {"entities" : qUnion([Q0]), "depth" : 25.4 * mm});
        }
        {
            var Q0;
            {var subQ0=sQuery(id+"F0.wireOp",EDGE,"E37");var subQ1=sQuery(id+"F0.wireOp",EDGE,"E0");var subQ5=makeQuery(id+"F0.imprint","INTERSECT",VERTEX,{"disambiguationData":[OD(0.0)],"derivedFrom":[subQ1,subQ0]});Q0=makeQuery(id+"F0.imprint","IMPRINT",FACE,{"disambiguationData":[TD([[makeQuery(id+"F0.imprint","IMPRINT",EDGE,{"disambiguationData":[TD([[subQ5,-1.0]])],"derivedFrom":subQ1}),-1.0]])]});}
            extrude(context, id + "F33", {"entities" : qUnion([Q0]), "depth" : 25.4 * mm});
        }
        {
            var Q0;
            {var subQ0=sQuery(id+"F0.wireOp",EDGE,"E41");var subQ1=sQuery(id+"F0.wireOp",EDGE,"E0");var subQ5=makeQuery(id+"F0.imprint","INTERSECT",VERTEX,{"disambiguationData":[OD(0.0)],"derivedFrom":[subQ1,subQ0]});Q0=makeQuery(id+"F0.imprint","IMPRINT",FACE,{"disambiguationData":[TD([[makeQuery(id+"F0.imprint","IMPRINT",EDGE,{"disambiguationData":[TD([[subQ5,-1.0]])],"derivedFrom":subQ1}),-1.0]])]});}
            extrude(context, id + "F34", {"entities" : qUnion([Q0]), "depth" : 25.4 * mm});
        }
        {
            var Q0;
            {var subQ0=sQuery(id+"F0.wireOp",EDGE,"E42");var subQ1=sQuery(id+"F0.wireOp",EDGE,"E0");var subQ5=makeQuery(id+"F0.imprint","INTERSECT",VERTEX,{"disambiguationData":[OD(0.0)],"derivedFrom":[subQ1,subQ0]});Q0=makeQuery(id+"F0.imprint","IMPRINT",FACE,{"disambiguationData":[TD([[makeQuery(id+"F0.imprint","IMPRINT",EDGE,{"disambiguationData":[TD([[subQ5,-1.0]])],"derivedFrom":subQ1}),-1.0]])]});}
            extrude(context, id + "F35", {"entities" : qUnion([Q0]), "depth" : 25.4 * mm});
        }
        {
            var Q0;
            {var subQ0=sQuery(id+"F0.wireOp",EDGE,"E43");var subQ1=sQuery(id+"F0.wireOp",EDGE,"E0");var subQ2=makeQuery(id+"F0.imprint","INTERSECT",VERTEX,{"disambiguationData":[OD(1.0)],"derivedFrom":[subQ1,subQ0]});Q0=makeQuery(id+"F0.imprint","IMPRINT",FACE,{"disambiguationData":[TD([[makeQuery(id+"F0.imprint","IMPRINT",EDGE,{"disambiguationData":[TD([[subQ2,-1.0]])],"derivedFrom":subQ1}),-1.0]])]});}
            extrude(context, id + "F36", {"entities" : qUnion([Q0]), "operationType" : NewBodyOperationType.ADD, "depth" : 25.4 * mm});
        }
        {
            var Q0;
            {var subQ0=sQuery(id+"F0.wireOp",EDGE,"E40");var subQ2=sQuery(id+"F0.wireOp",EDGE,"E0");var subQ7=makeQuery(id+"F0.imprint","INTERSECT",VERTEX,{"disambiguationData":[OD(1.0)],"derivedFrom":[subQ2,subQ0]});Q0=makeQuery(id+"F0.imprint","IMPRINT",FACE,{"disambiguationData":[TD([[makeQuery(id+"F0.imprint","IMPRINT",EDGE,{"disambiguationData":[TD([[subQ7,-1.0]])],"derivedFrom":subQ2}),-1.0]])]});}
            extrude(context, id + "F37", {"entities" : qUnion([Q0]), "depth" : 25.4 * mm});
        }
        {
            var Q0;
            {var subQ0=sQuery(id+"F0.wireOp",EDGE,"E44");var subQ8=sQuery(id+"F0.wireOp",EDGE,"E0");var subQ9=makeQuery(id+"F0.imprint","INTERSECT",VERTEX,{"derivedFrom":[subQ8,subQ0]});Q0=makeQuery(id+"F0.imprint","IMPRINT",FACE,{"disambiguationData":[TD([[makeQuery(id+"F0.imprint","IMPRINT",EDGE,{"disambiguationData":[TD([[subQ9,-1.0]])],"derivedFrom":subQ8}),-1.0]])]});}
            extrude(context, id + "F38", {"entities" : qUnion([Q0]), "depth" : 25.4 * mm});
        }
        {
            var Q0;
            {var subQ0=sQuery(id+"F0.wireOp",EDGE,"E45");var subQ1=sQuery(id+"F0.wireOp",EDGE,"E43");var subQ2=makeQuery(id+"F0.imprint","INTERSECT",VERTEX,{"disambiguationData":[OD(0.0)],"derivedFrom":[subQ1,subQ0]});Q0=makeQuery(id+"F0.imprint","IMPRINT",FACE,{"disambiguationData":[TD([[makeQuery(id+"F0.imprint","IMPRINT",EDGE,{"disambiguationData":[TD([[subQ2,-1.0]])],"derivedFrom":subQ1}),-1.0]])]});}
            extrude(context, id + "F39", {"entities" : qUnion([Q0]), "depth" : 25.4 * mm});
        }
        {
            var Q0;
            {var subQ0=sQuery(id+"F0.wireOp",EDGE,"E46");var subQ3=sQuery(id+"F0.wireOp",EDGE,"E0");var subQ9=makeQuery(id+"F0.imprint","INTERSECT",VERTEX,{"disambiguationData":[OD(0.0)],"derivedFrom":[subQ3,subQ0]});Q0=makeQuery(id+"F0.imprint","IMPRINT",FACE,{"disambiguationData":[TD([[makeQuery(id+"F0.imprint","IMPRINT",EDGE,{"disambiguationData":[TD([[subQ9,1.0]])],"derivedFrom":subQ3}),-1.0]])]});}
            extrude(context, id + "F40", {"entities" : qUnion([Q0]), "depth" : 25.4 * mm});
        }
        {
            var Q0;
            {var subQ0=sQuery(id+"F0.wireOp",EDGE,"E12");var subQ1=sQuery(id+"F0.wireOp",EDGE,"E11");var subQ2=makeQuery(id+"F0.imprint","INTERSECT",VERTEX,{"disambiguationData":[OD(1.0)],"derivedFrom":[subQ1,subQ0]});Q0=makeQuery(id+"F0.imprint","IMPRINT",FACE,{"disambiguationData":[TD([[makeQuery(id+"F0.imprint","IMPRINT",EDGE,{"disambiguationData":[TD([[subQ2,-1.0]])],"derivedFrom":subQ1}),1.0]])]});}
            extrude(context, id + "F41", {"entities" : qUnion([Q0]), "depth" : 25.4 * mm});
        }
        {
            var Q0;
            {var subQ0=sQuery(id+"F0.wireOp",EDGE,"E21");var subQ1=sQuery(id+"F0.wireOp",EDGE,"E20");var subQ2=makeQuery(id+"F0.imprint","INTERSECT",VERTEX,{"disambiguationData":[OD(1.0)],"derivedFrom":[subQ1,subQ0]});Q0=makeQuery(id+"F0.imprint","IMPRINT",FACE,{"disambiguationData":[TD([[makeQuery(id+"F0.imprint","IMPRINT",EDGE,{"disambiguationData":[TD([[subQ2,-1.0]])],"derivedFrom":subQ1}),-1.0]])]});}
            extrude(context, id + "F42", {"entities" : qUnion([Q0]), "depth" : 25.4 * mm});
        }
        {
            var Q0;
            {var subQ0=sQuery(id+"F0.wireOp",EDGE,"E12");var subQ1=sQuery(id+"F0.wireOp",EDGE,"E11");var subQ2=makeQuery(id+"F0.imprint","INTERSECT",VERTEX,{"disambiguationData":[OD(1.0)],"derivedFrom":[subQ1,subQ0]});Q0=makeQuery(id+"F0.imprint","IMPRINT",FACE,{"disambiguationData":[TD([[makeQuery(id+"F0.imprint","IMPRINT",EDGE,{"disambiguationData":[TD([[subQ2,-1.0]])],"derivedFrom":subQ1}),1.0]])]});}
            extrude(context, id + "F43", {"entities" : qUnion([Q0]), "depth" : 25.4 * mm});
        }
        {
            var Q0;
            {var subQ0=sQuery(id+"F0.wireOp",EDGE,"E22");var subQ1=sQuery(id+"F0.wireOp",EDGE,"E0");var subQ2=makeQuery(id+"F0.imprint","INTERSECT",VERTEX,{"disambiguationData":[OD(1.0)],"derivedFrom":[subQ1,subQ0]});Q0=makeQuery(id+"F0.imprint","IMPRINT",FACE,{"disambiguationData":[TD([[makeQuery(id+"F0.imprint","IMPRINT",EDGE,{"disambiguationData":[TD([[subQ2,-1.0]])],"derivedFrom":subQ1}),-1.0]])]});}
            extrude(context, id + "F44", {"entities" : qUnion([Q0]), "depth" : 25.4 * mm});
        }
        {
            var Q0;
            {var subQ0=sQuery(id+"F0.wireOp",EDGE,"E26");var subQ1=sQuery(id+"F0.wireOp",EDGE,"E19");var subQ2=makeQuery(id+"F0.imprint","INTERSECT",VERTEX,{"disambiguationData":[OD(0.0)],"derivedFrom":[subQ1,subQ0]});Q0=makeQuery(id+"F0.imprint","IMPRINT",FACE,{"disambiguationData":[TD([[makeQuery(id+"F0.imprint","IMPRINT",EDGE,{"disambiguationData":[TD([[subQ2,-1.0]])],"derivedFrom":subQ1}),1.0]])]});}
            extrude(context, id + "F45", {"entities" : qUnion([Q0]), "depth" : 25.4 * mm});
        }
        {
            var Q0;
            {var subQ0=sQuery(id+"F0.wireOp",EDGE,"E17");var subQ4=sQuery(id+"F0.wireOp",EDGE,"E9");var subQ5=makeQuery(id+"F0.imprint","INTERSECT",VERTEX,{"disambiguationData":[OD(0.0)],"derivedFrom":[subQ4,subQ0]});Q0=makeQuery(id+"F0.imprint","IMPRINT",FACE,{"disambiguationData":[TD([[makeQuery(id+"F0.imprint","IMPRINT",EDGE,{"disambiguationData":[TD([[subQ5,-1.0]])],"derivedFrom":subQ4}),-1.0]])]});}
            extrude(context, id + "F46", {"entities" : qUnion([Q0]), "depth" : 25.4 * mm});
        }
        {
            var Q0;
            {var subQ1=sQuery(id+"F0.wireOp",EDGE,"E12");var subQ10=sQuery(id+"F0.wireOp",EDGE,"E10");var subQ17=makeQuery(id+"F0.imprint","INTERSECT",VERTEX,{"disambiguationData":[OD(0.0)],"derivedFrom":[subQ10,subQ1]});Q0=makeQuery(id+"F0.imprint","IMPRINT",FACE,{"disambiguationData":[TD([[makeQuery(id+"F0.imprint","IMPRINT",EDGE,{"disambiguationData":[TD([[subQ17,-1.0]])],"derivedFrom":subQ10}),-1.0]])]});}
            extrude(context, id + "F47", {"entities" : qUnion([Q0]), "depth" : 25.4 * mm});
        }
        {
            var Q0;
            {var subQ1=sQuery(id+"F0.wireOp",EDGE,"E1");var subQ7=sQuery(id+"F0.wireOp",EDGE,"E0");var subQ21=makeQuery(id+"F0.imprint","INTERSECT",VERTEX,{"disambiguationData":[OD(0.0)],"derivedFrom":[subQ7,subQ1]});Q0=makeQuery(id+"F0.imprint","IMPRINT",FACE,{"disambiguationData":[TD([[makeQuery(id+"F0.imprint","IMPRINT",EDGE,{"disambiguationData":[TD([[subQ21,-1.0]])],"derivedFrom":subQ7}),-1.0]])]});}
            extrude(context, id + "F48", {"entities" : qUnion([Q0]), "depth" : 25.4 * mm});
        }
    });
